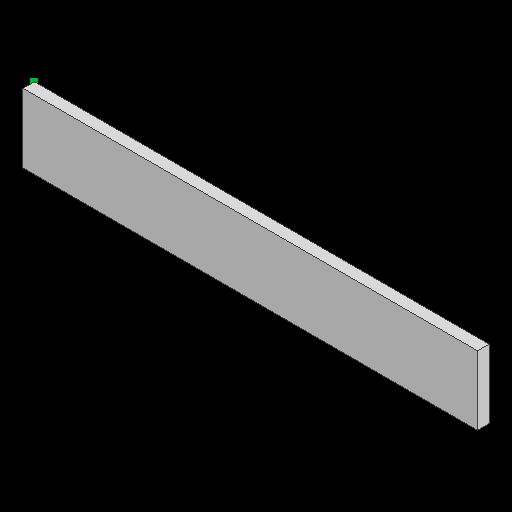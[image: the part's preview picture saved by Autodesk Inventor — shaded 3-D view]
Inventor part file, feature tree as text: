
AUTODESK INVENTOR PART (.ipt)
format: ipt  version: 2025.1 (Build 291241000, 241)  size: 148,992 bytes
history: native  units: in
note: dims shown in document units (in); Inventor stores cm internally (conversion verified against a paired STEP export)
features: sketch x3, other x2, extrude x2, projected_geometry x1
ambient origin geometry x8: Origin, YZ Plane, XZ Plane, XY Plane, X Axis, Y Axis, Z Axis, Center Point
bodies: Body1 (feature_tree)
feature tree (8):
  other  "솔리드1"
  sketch  "스케치1"
  extrude  "돌출1"  Depth=7.7953in
  extrude  "돌출2"  Depth=1.1811in
  sketch  "스케치2"
  other  "스케치 - 직사각형 패턴1"
  sketch  "스케치3"
  projected_geometry  "투영된 루프1"
